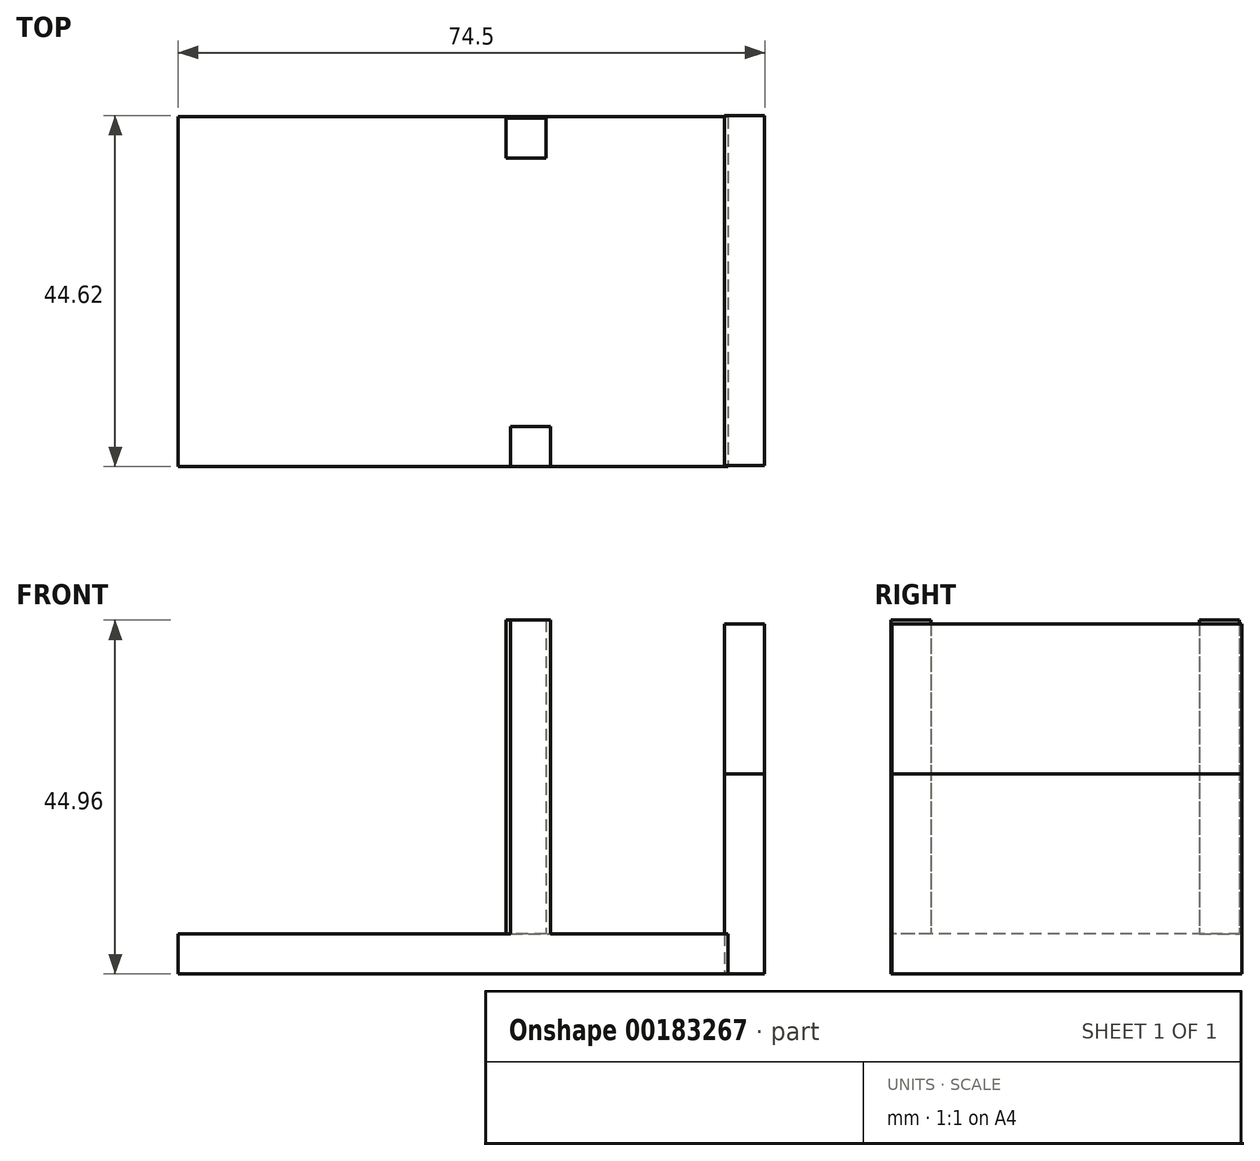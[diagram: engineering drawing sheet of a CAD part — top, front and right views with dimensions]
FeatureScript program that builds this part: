
annotation { "Feature Type Name" : "Feature", "Feature Type Description" : "" }
export const myFeature = defineFeature(function(context is Context, id is Id, definition is map)
    precondition{}
    {
        {
            var Q0;
            Q0=qCreatedBy(makeId("Top.planeOp"),FACE);
            var sketch = newSketch(context, id + "F0", { "sketchPlane" : qUnion([Q0])});
            skLineSegment(sketch, "E0.bottom", {"start": v(-34.93, 22.23) * mm, "end": v(34.93, 22.23) * mm});
            skLineSegment(sketch, "E0.top", {"start": v(-34.93, -22.22) * mm, "end": v(34.92, -22.22) * mm});
            skLineSegment(sketch, "E0.left", {"start": v(-34.92, 22.23) * mm, "end": v(-34.93, -22.22) * mm});
            skLineSegment(sketch, "E0.right", {"start": v(34.93, 22.23) * mm, "end": v(34.92, -22.22) * mm});
            skPoint(sketch, "E0.middle", {"position": v(0, 0) * mm});
            skSolve(sketch);
        }
        {
            var Q0;
            Q0 = qSketchRegion(id + "F0", true);
            extrude(context, id + "F1", {"entities" : qUnion([Q0]), "depth" : 5.08 * mm});
        }
        {
            var Q0;
            Q0=qCreatedBy(makeId("Top.planeOp"),FACE);
            var sketch = newSketch(context, id + "F2", { "sketchPlane" : qUnion([Q0])});
            skLineSegment(sketch, "E1.bottom", {"start": v(34.49, -22.06) * mm, "end": v(39.57, -22.06) * mm});
            skLineSegment(sketch, "E1.top", {"start": v(34.49, 22.39) * mm, "end": v(39.57, 22.39) * mm});
            skLineSegment(sketch, "E1.left", {"start": v(34.49, -22.06) * mm, "end": v(34.49, 22.39) * mm});
            skLineSegment(sketch, "E1.right", {"start": v(39.57, -22.06) * mm, "end": v(39.57, 22.39) * mm});
            skSolve(sketch);
        }
        {
            var Q0;
            Q0 = qSketchRegion(id + "F2", true);
            extrude(context, id + "F3", {"entities" : qUnion([Q0]), "depth" : 44.45 * mm});
        }
        {
            var Q0;
            Q0 = qSketchRegion(id + "F2", true);
            extrude(context, id + "F4", {"entities" : qUnion([Q0]), "depth" : 25.4 * mm});
        }
        {
            var Q0;
            Q0=qCreatedBy(makeId("Top.planeOp"),FACE);
            var sketch = newSketch(context, id + "F5", { "sketchPlane" : qUnion([Q0])});
            skLineSegment(sketch, "E2.bottom", {"start": v(12.37, -22.22) * mm, "end": v(7.29, -22.22) * mm});
            skLineSegment(sketch, "E2.top", {"start": v(12.37, -17.14) * mm, "end": v(7.29, -17.14) * mm});
            skLineSegment(sketch, "E2.left", {"start": v(12.37, -22.22) * mm, "end": v(12.37, -17.14) * mm});
            skLineSegment(sketch, "E2.right", {"start": v(7.29, -22.22) * mm, "end": v(7.29, -17.14) * mm});
            skSolve(sketch);
        }
        {
            var Q0;
            Q0 = qSketchRegion(id + "F5", true);
            extrude(context, id + "F6", {"entities" : qUnion([Q0]), "operationType" : NewBodyOperationType.ADD, "depth" : 44.96 * mm});
        }
        {
            var Q0;
            Q0=qCreatedBy(makeId("Top.planeOp"),FACE);
            var sketch = newSketch(context, id + "F7", { "sketchPlane" : qUnion([Q0])});
            skLineSegment(sketch, "E3.bottom", {"start": v(6.72, 22.04) * mm, "end": v(11.8, 22.04) * mm});
            skLineSegment(sketch, "E3.top", {"start": v(6.72, 16.96) * mm, "end": v(11.8, 16.96) * mm});
            skLineSegment(sketch, "E3.left", {"start": v(6.72, 22.04) * mm, "end": v(6.72, 16.96) * mm});
            skLineSegment(sketch, "E3.right", {"start": v(11.8, 22.04) * mm, "end": v(11.8, 16.96) * mm});
            skSolve(sketch);
        }
        {
            var Q0;
            Q0 = qSketchRegion(id + "F7", true);
            var Q1;
            Q1 = qSketchRegion(id + "F5", true);
            extrude(context, id + "F8", {"entities" : qUnion([Q0, Q1]), "operationType" : NewBodyOperationType.ADD, "depth" : 44.96 * mm});
        }
    });
